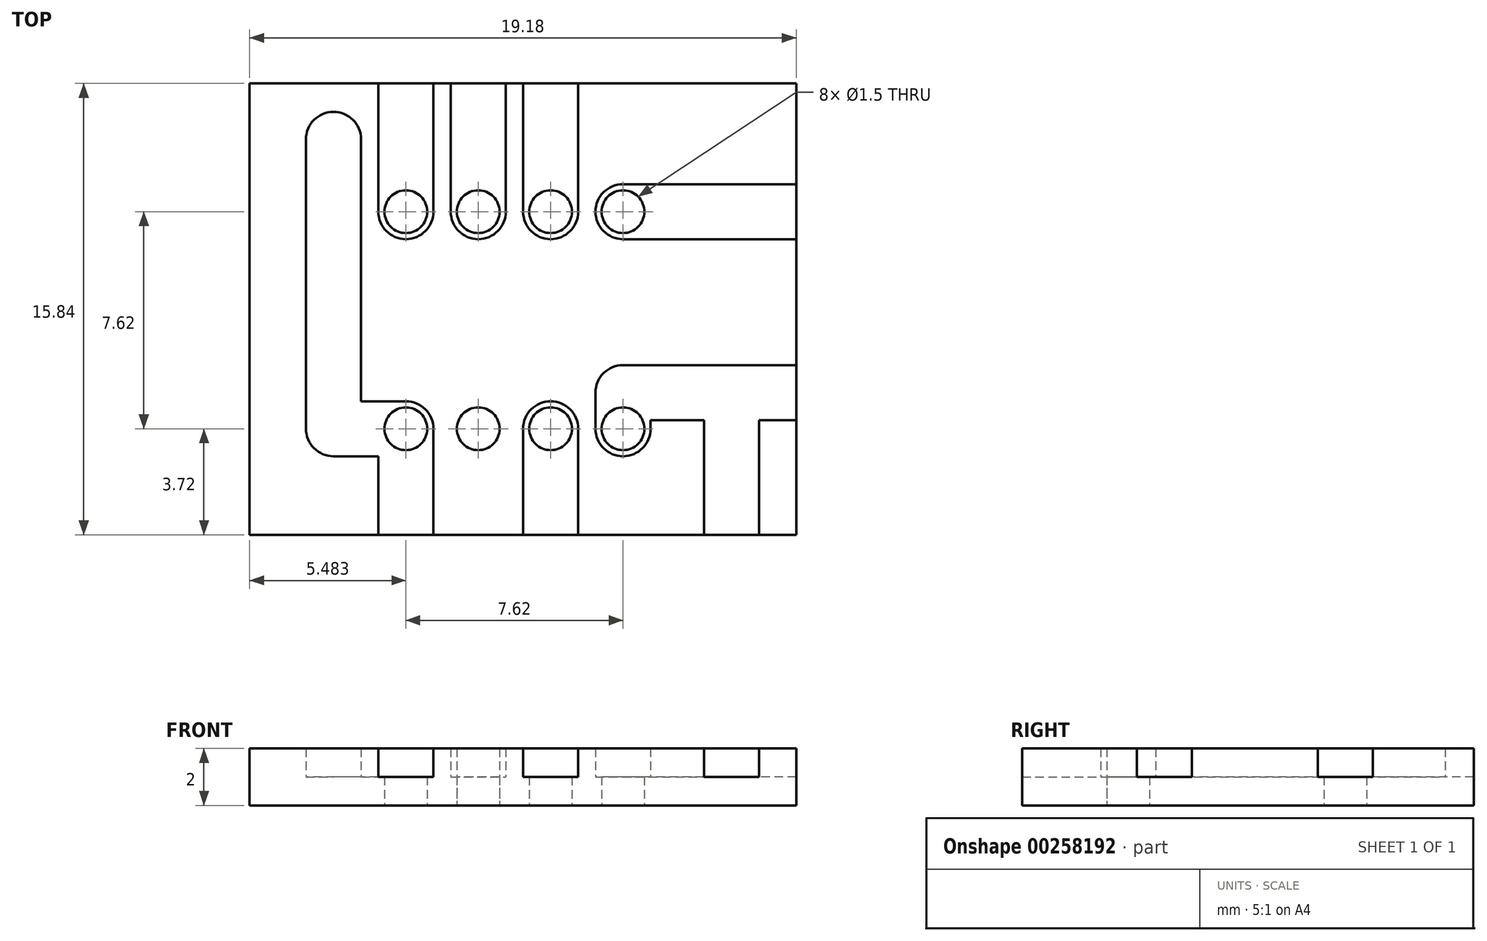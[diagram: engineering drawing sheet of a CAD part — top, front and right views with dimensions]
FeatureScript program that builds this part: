
annotation { "Feature Type Name" : "Feature", "Feature Type Description" : "" }
export const myFeature = defineFeature(function(context is Context, id is Id, definition is map)
    precondition{}
    {
        {
            var Q0;
            Q0=qCreatedBy(makeId("Top.planeOp"),FACE);
            var sketch = newSketch(context, id + "F0", { "sketchPlane" : qUnion([Q0])});
            skArc(sketch, "E0", {"start": v(-10.18, 10.53) * mm, "mid": v(-9.22, 9.56) * mm, "end": v(-8.25, 10.53) * mm});
            skLineSegment(sketch, "E1", {"start": v(-9.22, 9.56) * mm, "end": v(-2.87, 9.56) * mm});
            skArc(sketch, "E2", {"start": v(-2.87, 9.56) * mm, "mid": v(-1.9, 10.53) * mm, "end": v(-2.87, 11.5) * mm});
            skLineSegment(sketch, "E3", {"start": v(-2.87, 11.5) * mm, "end": v(-9.22, 11.5) * mm});
            skArc(sketch, "E4", {"start": v(-9.22, 11.5) * mm, "mid": v(-10.18, 10.53) * mm, "end": v(-9.22, 9.56) * mm});
            skArc(sketch, "E5", {"start": v(-3.83, 10.53) * mm, "mid": v(-2.87, 9.56) * mm, "end": v(-1.9, 10.53) * mm});
            skArc(sketch, "E6", {"start": v(3.79, 10.53) * mm, "mid": v(4.75, 9.56) * mm, "end": v(5.72, 10.53) * mm});
            skArc(sketch, "E7", {"start": v(16.49, 2.9) * mm, "mid": v(17.45, 1.94) * mm, "end": v(18.42, 2.9) * mm});
            skLineSegment(sketch, "E8", {"start": v(17.45, 1.94) * mm, "end": v(20, 1.94) * mm});
            skArc(sketch, "E9", {"start": v(20, 1.94) * mm, "mid": v(20.96, 2.9) * mm, "end": v(20, 3.88) * mm});
            skLineSegment(sketch, "E10", {"start": v(20, 3.88) * mm, "end": v(17.45, 3.88) * mm});
            skArc(sketch, "E11", {"start": v(17.45, 3.88) * mm, "mid": v(16.49, 2.9) * mm, "end": v(17.45, 1.94) * mm});
            skLineSegment(sketch, "E12", {"start": v(19.03, 2.9) * mm, "end": v(19.03, -12.33) * mm});
            skArc(sketch, "E13", {"start": v(19.03, -12.33) * mm, "mid": v(20, -13.3) * mm, "end": v(20.96, -12.33) * mm});
            skLineSegment(sketch, "E14", {"start": v(20.96, -12.33) * mm, "end": v(20.96, 2.9) * mm});
            skArc(sketch, "E15", {"start": v(20.96, 2.9) * mm, "mid": v(20, 3.88) * mm, "end": v(19.03, 2.9) * mm});
            skLineSegment(sketch, "E16", {"start": v(20, -11.36) * mm, "end": v(17.45, -11.36) * mm});
            skArc(sketch, "E17", {"start": v(17.45, -11.36) * mm, "mid": v(16.49, -12.33) * mm, "end": v(17.45, -13.3) * mm});
            skLineSegment(sketch, "E18", {"start": v(17.45, -13.3) * mm, "end": v(20, -13.3) * mm});
            skArc(sketch, "E19", {"start": v(20, -13.3) * mm, "mid": v(20.96, -12.33) * mm, "end": v(20, -11.36) * mm});
            skLineSegment(sketch, "E20", {"start": v(-3.83, 10.53) * mm, "end": v(-3.83, 4.18) * mm});
            skArc(sketch, "E21", {"start": v(-3.83, 4.18) * mm, "mid": v(-2.87, 3.21) * mm, "end": v(-1.9, 4.18) * mm});
            skLineSegment(sketch, "E22", {"start": v(-1.9, 4.18) * mm, "end": v(-1.9, 10.53) * mm});
            skArc(sketch, "E23", {"start": v(-1.9, 10.53) * mm, "mid": v(-2.87, 11.5) * mm, "end": v(-3.83, 10.53) * mm});
            skArc(sketch, "E24", {"start": v(-5.4, 5.75) * mm, "mid": v(-4.44, 6.72) * mm, "end": v(-5.4, 7.69) * mm});
            skLineSegment(sketch, "E25", {"start": v(-6.37, 6.72) * mm, "end": v(-6.37, -3.44) * mm});
            skArc(sketch, "E26", {"start": v(-6.37, -3.44) * mm, "mid": v(-5.4, -4.4) * mm, "end": v(-4.44, -3.44) * mm});
            skLineSegment(sketch, "E27", {"start": v(-4.44, -3.44) * mm, "end": v(-4.44, 6.72) * mm});
            skArc(sketch, "E28", {"start": v(-4.44, 6.72) * mm, "mid": v(-5.4, 7.69) * mm, "end": v(-6.37, 6.72) * mm});
            skLineSegment(sketch, "E29", {"start": v(-5.4, -4.4) * mm, "end": v(-2.87, -4.4) * mm});
            skArc(sketch, "E30", {"start": v(-2.87, -4.4) * mm, "mid": v(-1.9, -3.44) * mm, "end": v(-2.87, -2.47) * mm});
            skLineSegment(sketch, "E31", {"start": v(-2.87, -2.47) * mm, "end": v(-5.4, -2.47) * mm});
            skArc(sketch, "E32", {"start": v(-5.4, -2.47) * mm, "mid": v(-6.37, -3.44) * mm, "end": v(-5.4, -4.4) * mm});
            skLineSegment(sketch, "E33", {"start": v(-3.83, -3.44) * mm, "end": v(-3.83, -8.52) * mm});
            skArc(sketch, "E34", {"start": v(-3.83, -8.52) * mm, "mid": v(-2.87, -9.49) * mm, "end": v(-1.9, -8.52) * mm});
            skLineSegment(sketch, "E35", {"start": v(-1.9, -8.52) * mm, "end": v(-1.9, -3.44) * mm});
            skArc(sketch, "E36", {"start": v(-1.9, -3.44) * mm, "mid": v(-2.87, -2.47) * mm, "end": v(-3.83, -3.44) * mm});
            skLineSegment(sketch, "E37", {"start": v(-3.83, -8.52) * mm, "end": v(-3.83, -13.6) * mm});
            skArc(sketch, "E38", {"start": v(-3.83, -13.6) * mm, "mid": v(-2.87, -14.57) * mm, "end": v(-1.9, -13.6) * mm});
            skLineSegment(sketch, "E39", {"start": v(-1.9, -13.6) * mm, "end": v(-1.9, -8.52) * mm});
            skArc(sketch, "E40", {"start": v(-1.9, -8.52) * mm, "mid": v(-2.87, -7.55) * mm, "end": v(-3.83, -8.52) * mm});
            skLineSegment(sketch, "E41", {"start": v(4.75, 3.21) * mm, "end": v(12.37, 3.21) * mm});
            skArc(sketch, "E42", {"start": v(12.37, 3.21) * mm, "mid": v(13.34, 4.18) * mm, "end": v(12.37, 5.15) * mm});
            skLineSegment(sketch, "E43", {"start": v(12.37, 5.15) * mm, "end": v(4.75, 5.15) * mm});
            skArc(sketch, "E44", {"start": v(4.75, 5.15) * mm, "mid": v(3.79, 4.18) * mm, "end": v(4.75, 3.21) * mm});
            skLineSegment(sketch, "E45", {"start": v(13.34, 4.18) * mm, "end": v(13.34, 10.53) * mm});
            skArc(sketch, "E46", {"start": v(13.34, 10.53) * mm, "mid": v(12.37, 11.5) * mm, "end": v(11.4, 10.53) * mm});
            skLineSegment(sketch, "E47", {"start": v(11.4, 10.53) * mm, "end": v(11.4, 4.18) * mm});
            skArc(sketch, "E48", {"start": v(11.4, 4.18) * mm, "mid": v(12.37, 3.21) * mm, "end": v(13.34, 4.18) * mm});
            skLineSegment(sketch, "E49", {"start": v(0.64, 4.18) * mm, "end": v(0.64, 10.53) * mm});
            skArc(sketch, "E50", {"start": v(0.64, 10.53) * mm, "mid": v(-0.33, 11.5) * mm, "end": v(-1.3, 10.53) * mm});
            skLineSegment(sketch, "E51", {"start": v(-1.3, 10.53) * mm, "end": v(-1.3, 4.18) * mm});
            skArc(sketch, "E52", {"start": v(-1.3, 4.18) * mm, "mid": v(-0.33, 3.21) * mm, "end": v(0.64, 4.18) * mm});
            skLineSegment(sketch, "E53", {"start": v(1.25, 10.53) * mm, "end": v(1.25, 4.18) * mm});
            skArc(sketch, "E54", {"start": v(1.25, 4.18) * mm, "mid": v(2.21, 3.21) * mm, "end": v(3.18, 4.18) * mm});
            skLineSegment(sketch, "E55", {"start": v(3.18, 4.18) * mm, "end": v(3.18, 10.53) * mm});
            skArc(sketch, "E56", {"start": v(3.18, 10.53) * mm, "mid": v(2.21, 11.5) * mm, "end": v(1.25, 10.53) * mm});
            skLineSegment(sketch, "E57", {"start": v(1.25, -3.44) * mm, "end": v(1.25, -8.52) * mm});
            skArc(sketch, "E58", {"start": v(1.25, -8.52) * mm, "mid": v(2.21, -9.49) * mm, "end": v(3.18, -8.52) * mm});
            skLineSegment(sketch, "E59", {"start": v(3.18, -8.52) * mm, "end": v(3.18, -3.44) * mm});
            skArc(sketch, "E60", {"start": v(3.18, -3.44) * mm, "mid": v(2.21, -2.47) * mm, "end": v(1.25, -3.44) * mm});
            skLineSegment(sketch, "E61", {"start": v(1.25, -8.52) * mm, "end": v(1.25, -17.41) * mm});
            skArc(sketch, "E62", {"start": v(1.25, -17.41) * mm, "mid": v(2.21, -18.38) * mm, "end": v(3.18, -17.41) * mm});
            skLineSegment(sketch, "E63", {"start": v(3.18, -17.41) * mm, "end": v(3.18, -8.52) * mm});
            skArc(sketch, "E64", {"start": v(3.18, -8.52) * mm, "mid": v(2.21, -7.55) * mm, "end": v(1.25, -8.52) * mm});
            skLineSegment(sketch, "E65", {"start": v(2.21, -18.38) * mm, "end": v(17.45, -18.38) * mm});
            skArc(sketch, "E66", {"start": v(17.45, -18.38) * mm, "mid": v(18.42, -17.41) * mm, "end": v(17.45, -16.44) * mm});
            skLineSegment(sketch, "E67", {"start": v(17.45, -16.44) * mm, "end": v(2.21, -16.44) * mm});
            skArc(sketch, "E68", {"start": v(2.21, -16.44) * mm, "mid": v(1.25, -17.41) * mm, "end": v(2.21, -18.38) * mm});
            skLineSegment(sketch, "E69", {"start": v(4.75, -7.55) * mm, "end": v(2.21, -7.55) * mm});
            skArc(sketch, "E70", {"start": v(2.21, -7.55) * mm, "mid": v(1.25, -8.52) * mm, "end": v(2.21, -9.49) * mm});
            skLineSegment(sketch, "E71", {"start": v(2.21, -9.49) * mm, "end": v(4.75, -9.49) * mm});
            skArc(sketch, "E72", {"start": v(4.75, -9.49) * mm, "mid": v(5.72, -8.52) * mm, "end": v(4.75, -7.55) * mm});
            skLineSegment(sketch, "E73", {"start": v(17.45, -1.2) * mm, "end": v(8.56, -1.2) * mm});
            skArc(sketch, "E74", {"start": v(8.56, -1.2) * mm, "mid": v(7.6, -2.17) * mm, "end": v(8.56, -3.14) * mm});
            skLineSegment(sketch, "E75", {"start": v(8.56, -3.14) * mm, "end": v(17.45, -3.14) * mm});
            skArc(sketch, "E76", {"start": v(17.45, -3.14) * mm, "mid": v(18.42, -2.17) * mm, "end": v(17.45, -1.2) * mm});
            skLineSegment(sketch, "E77", {"start": v(8.56, -1.2) * mm, "end": v(4.75, -1.2) * mm});
            skArc(sketch, "E78", {"start": v(4.75, -1.2) * mm, "mid": v(3.79, -2.17) * mm, "end": v(4.75, -3.14) * mm});
            skLineSegment(sketch, "E79", {"start": v(4.75, -3.14) * mm, "end": v(8.56, -3.14) * mm});
            skArc(sketch, "E80", {"start": v(8.56, -3.14) * mm, "mid": v(9.53, -2.17) * mm, "end": v(8.56, -1.2) * mm});
            skLineSegment(sketch, "E81", {"start": v(3.79, -2.17) * mm, "end": v(3.79, -3.44) * mm});
            skArc(sketch, "E82", {"start": v(3.79, -3.44) * mm, "mid": v(4.75, -4.4) * mm, "end": v(5.72, -3.44) * mm});
            skLineSegment(sketch, "E83", {"start": v(5.72, -3.44) * mm, "end": v(5.72, -2.17) * mm});
            skArc(sketch, "E84", {"start": v(5.72, -2.17) * mm, "mid": v(4.75, -1.2) * mm, "end": v(3.79, -2.17) * mm});
            skLineSegment(sketch, "E85", {"start": v(4.75, -14.57) * mm, "end": v(8.56, -14.57) * mm});
            skArc(sketch, "E86", {"start": v(8.56, -14.57) * mm, "mid": v(9.53, -13.6) * mm, "end": v(8.56, -12.63) * mm});
            skLineSegment(sketch, "E87", {"start": v(8.56, -12.63) * mm, "end": v(4.75, -12.63) * mm});
            skArc(sketch, "E88", {"start": v(4.75, -12.63) * mm, "mid": v(3.79, -13.6) * mm, "end": v(4.75, -14.57) * mm});
            skLineSegment(sketch, "E89", {"start": v(9.53, -13.6) * mm, "end": v(9.53, -2.17) * mm});
            skArc(sketch, "E90", {"start": v(9.53, -2.17) * mm, "mid": v(8.56, -1.2) * mm, "end": v(7.6, -2.17) * mm});
            skLineSegment(sketch, "E91", {"start": v(7.6, -2.17) * mm, "end": v(7.6, -13.6) * mm});
            skArc(sketch, "E92", {"start": v(7.6, -13.6) * mm, "mid": v(8.56, -14.57) * mm, "end": v(9.53, -13.6) * mm});
            skLineSegment(sketch, "E93", {"start": v(-2.87, -3.44) * mm, "end": v(2.21, -3.44) * mm, "construction": true});
            skPoint(sketch, "E94", {"position": v(-0.33, -3.44) * mm});
            skCircle(sketch, "E95", {"center": v(-2.87, -3.44) * mm, "radius": 0.75 * mm});
            skCircle(sketch, "E96", {"center": v(-0.33, -3.44) * mm, "radius": 0.75 * mm});
            skCircle(sketch, "E97", {"center": v(2.21, -3.44) * mm, "radius": 0.75 * mm});
            skCircle(sketch, "E98", {"center": v(4.75, -3.44) * mm, "radius": 0.75 * mm});
            skCircle(sketch, "E99", {"center": v(-2.87, 4.18) * mm, "radius": 0.75 * mm});
            skCircle(sketch, "E100", {"center": v(-0.33, 4.18) * mm, "radius": 0.75 * mm});
            skCircle(sketch, "E101", {"center": v(2.21, 4.18) * mm, "radius": 0.75 * mm});
            skCircle(sketch, "E102", {"center": v(4.75, 4.18) * mm, "radius": 0.75 * mm});
            skLineSegment(sketch, "E103.bottom", {"start": v(-8.35, 8.68) * mm, "end": v(10.83, 8.68) * mm});
            skLineSegment(sketch, "E103.top", {"start": v(-8.35, -7.16) * mm, "end": v(10.83, -7.16) * mm});
            skLineSegment(sketch, "E103.left", {"start": v(-8.35, 8.68) * mm, "end": v(-8.35, -7.16) * mm});
            skLineSegment(sketch, "E103.right", {"start": v(10.83, 8.68) * mm, "end": v(10.83, -7.16) * mm});
            skSolve(sketch);
        }
        {
            var Q0;
            {var subQ15=sQuery(id+"F0.wireOp",EDGE,"E21");Q0=makeQuery(id+"F0.imprint","IMPRINT",FACE,{"disambiguationData":[TD([[makeQuery(id+"F0.imprint","IMPRINT",EDGE,{"derivedFrom":subQ15}),-1.0]])]});}
            var Q1;
            {var subQ0=sQuery(id+"F0.wireOp",EDGE,"E103.right");var subQ1=sQuery(id+"F0.wireOp",EDGE,"E75");var subQ2=makeQuery(id+"F0.imprint","INTERSECT",VERTEX,{"derivedFrom":[subQ1,subQ0]});Q1=makeQuery(id+"F0.imprint","IMPRINT",FACE,{"disambiguationData":[TD([[makeQuery(id+"F0.imprint","IMPRINT",EDGE,{"disambiguationData":[TD([[subQ2,1.0]])],"derivedFrom":subQ1}),-1.0]])]});}
            var Q2;
            {var subQ6=sQuery(id+"F0.wireOp",EDGE,"E25");Q2=makeQuery(id+"F0.imprint","IMPRINT",FACE,{"disambiguationData":[TD([[makeQuery(id+"F0.imprint","IMPRINT",EDGE,{"derivedFrom":subQ6}),1.0]])]});}
            var Q3;
            {var subQ5=sQuery(id+"F0.wireOp",EDGE,"E26");Q3=makeQuery(id+"F0.imprint","IMPRINT",FACE,{"disambiguationData":[TD([[makeQuery(id+"F0.imprint","IMPRINT",EDGE,{"derivedFrom":subQ5}),1.0]])]});}
            var Q4;
            {var subQ7=sQuery(id+"F0.wireOp",EDGE,"E26");Q4=makeQuery(id+"F0.imprint","IMPRINT",FACE,{"disambiguationData":[TD([[makeQuery(id+"F0.imprint","IMPRINT",EDGE,{"derivedFrom":subQ7}),-1.0]])]});}
            var Q5;
            {var subQ1=sQuery(id+"F0.wireOp",EDGE,"E30");Q5=makeQuery(id+"F0.imprint","IMPRINT",FACE,{"disambiguationData":[TD([[makeQuery(id+"F0.imprint","IMPRINT",EDGE,{"derivedFrom":subQ1}),1.0]])]});}
            var Q6;
            {var subQ6=sQuery(id+"F0.wireOp",EDGE,"E30");Q6=makeQuery(id+"F0.imprint","IMPRINT",FACE,{"disambiguationData":[TD([[makeQuery(id+"F0.imprint","IMPRINT",EDGE,{"derivedFrom":subQ6}),-1.0]])]});}
            var Q7;
            {var subQ0=sQuery(id+"F0.wireOp",EDGE,"E60");Q7=makeQuery(id+"F0.imprint","IMPRINT",FACE,{"disambiguationData":[TD([[makeQuery(id+"F0.imprint","IMPRINT",EDGE,{"derivedFrom":subQ0}),1.0]])]});}
            var Q8;
            {var subQ6=sQuery(id+"F0.wireOp",EDGE,"E98");var subQ8=sQuery(id+"F0.wireOp",EDGE,"E79");var subQ9=makeQuery(id+"F0.imprint","INTERSECT",VERTEX,{"derivedFrom":[subQ8,subQ6]});Q8=makeQuery(id+"F0.imprint","IMPRINT",FACE,{"disambiguationData":[TD([[makeQuery(id+"F0.imprint","IMPRINT",EDGE,{"disambiguationData":[TD([[subQ9,-1.0]])],"derivedFrom":subQ8}),1.0]])]});}
            var Q9;
            {var subQ0=sQuery(id+"F0.wireOp",EDGE,"E81");Q9=makeQuery(id+"F0.imprint","IMPRINT",FACE,{"disambiguationData":[TD([[makeQuery(id+"F0.imprint","IMPRINT",EDGE,{"derivedFrom":subQ0}),1.0]])]});}
            var Q10;
            {var subQ1=sQuery(id+"F0.wireOp",EDGE,"E77");Q10=makeQuery(id+"F0.imprint","IMPRINT",FACE,{"disambiguationData":[TD([[makeQuery(id+"F0.imprint","IMPRINT",EDGE,{"derivedFrom":subQ1}),1.0]])]});}
            var Q11;
            {var subQ3=sQuery(id+"F0.wireOp",EDGE,"E75");var subQ7=sQuery(id+"F0.wireOp",EDGE,"E103.right");var subQ8=makeQuery(id+"F0.imprint","INTERSECT",VERTEX,{"derivedFrom":[subQ3,subQ7]});Q11=makeQuery(id+"F0.imprint","IMPRINT",FACE,{"disambiguationData":[TD([[makeQuery(id+"F0.imprint","IMPRINT",EDGE,{"disambiguationData":[TD([[subQ8,1.0]])],"derivedFrom":subQ3}),1.0]])]});}
            var Q12;
            {var subQ0=sQuery(id+"F0.wireOp",EDGE,"E74");Q12=makeQuery(id+"F0.imprint","IMPRINT",FACE,{"disambiguationData":[TD([[makeQuery(id+"F0.imprint","IMPRINT",EDGE,{"derivedFrom":subQ0}),1.0]])]});}
            var Q13;
            {var subQ0=sQuery(id+"F0.wireOp",EDGE,"E103.top");var subQ5=sQuery(id+"F0.wireOp",EDGE,"E89");var subQ6=makeQuery(id+"F0.imprint","INTERSECT",VERTEX,{"derivedFrom":[subQ5,subQ0]});Q13=makeQuery(id+"F0.imprint","IMPRINT",FACE,{"disambiguationData":[TD([[makeQuery(id+"F0.imprint","IMPRINT",EDGE,{"disambiguationData":[TD([[subQ6,-1.0]])],"derivedFrom":subQ5}),1.0]])]});}
            var Q14;
            {var subQ0=sQuery(id+"F0.wireOp",EDGE,"E74");Q14=makeQuery(id+"F0.imprint","IMPRINT",FACE,{"disambiguationData":[TD([[makeQuery(id+"F0.imprint","IMPRINT",EDGE,{"derivedFrom":subQ0}),-1.0]])]});}
            var Q15;
            {var subQ0=sQuery(id+"F0.wireOp",EDGE,"E80");Q15=makeQuery(id+"F0.imprint","IMPRINT",FACE,{"disambiguationData":[TD([[makeQuery(id+"F0.imprint","IMPRINT",EDGE,{"derivedFrom":subQ0}),-1.0]])]});}
            var Q16;
            {var subQ0=sQuery(id+"F0.wireOp",EDGE,"E44");Q16=makeQuery(id+"F0.imprint","IMPRINT",FACE,{"disambiguationData":[TD([[makeQuery(id+"F0.imprint","IMPRINT",EDGE,{"derivedFrom":subQ0}),1.0]])]});}
            var Q17;
            {var subQ1=sQuery(id+"F0.wireOp",EDGE,"E54");Q17=makeQuery(id+"F0.imprint","IMPRINT",FACE,{"disambiguationData":[TD([[makeQuery(id+"F0.imprint","IMPRINT",EDGE,{"derivedFrom":subQ1}),1.0]])]});}
            var Q18;
            {var subQ0=sQuery(id+"F0.wireOp",EDGE,"E52");Q18=makeQuery(id+"F0.imprint","IMPRINT",FACE,{"disambiguationData":[TD([[makeQuery(id+"F0.imprint","IMPRINT",EDGE,{"derivedFrom":subQ0}),1.0]])]});}
            var Q19;
            {var subQ1=sQuery(id+"F0.wireOp",EDGE,"E21");Q19=makeQuery(id+"F0.imprint","IMPRINT",FACE,{"disambiguationData":[TD([[makeQuery(id+"F0.imprint","IMPRINT",EDGE,{"derivedFrom":subQ1}),1.0]])]});}
            extrude(context, id + "F1", {"entities" : qUnion([Q0, Q1, Q2, Q3, Q4, Q5, Q6, Q7, Q8, Q9, Q10, Q11, Q12, Q13, Q14, Q15, Q16, Q17, Q18, Q19]), "depth" : 1 * mm});
        }
        {
            var Q0;
            {var subQ15=sQuery(id+"F0.wireOp",EDGE,"E21");Q0=makeQuery(id+"F0.imprint","IMPRINT",FACE,{"disambiguationData":[TD([[makeQuery(id+"F0.imprint","IMPRINT",EDGE,{"derivedFrom":subQ15}),-1.0]])]});}
            var Q1;
            {var subQ0=sQuery(id+"F0.wireOp",EDGE,"E103.right");var subQ1=sQuery(id+"F0.wireOp",EDGE,"E75");var subQ2=makeQuery(id+"F0.imprint","INTERSECT",VERTEX,{"derivedFrom":[subQ1,subQ0]});Q1=makeQuery(id+"F0.imprint","IMPRINT",FACE,{"disambiguationData":[TD([[makeQuery(id+"F0.imprint","IMPRINT",EDGE,{"disambiguationData":[TD([[subQ2,1.0]])],"derivedFrom":subQ1}),-1.0]])]});}
            extrude(context, id + "F2", {"entities" : qUnion([Q0, Q1]), "operationType" : NewBodyOperationType.ADD, "depth" : 2 * mm});
        }
    });
